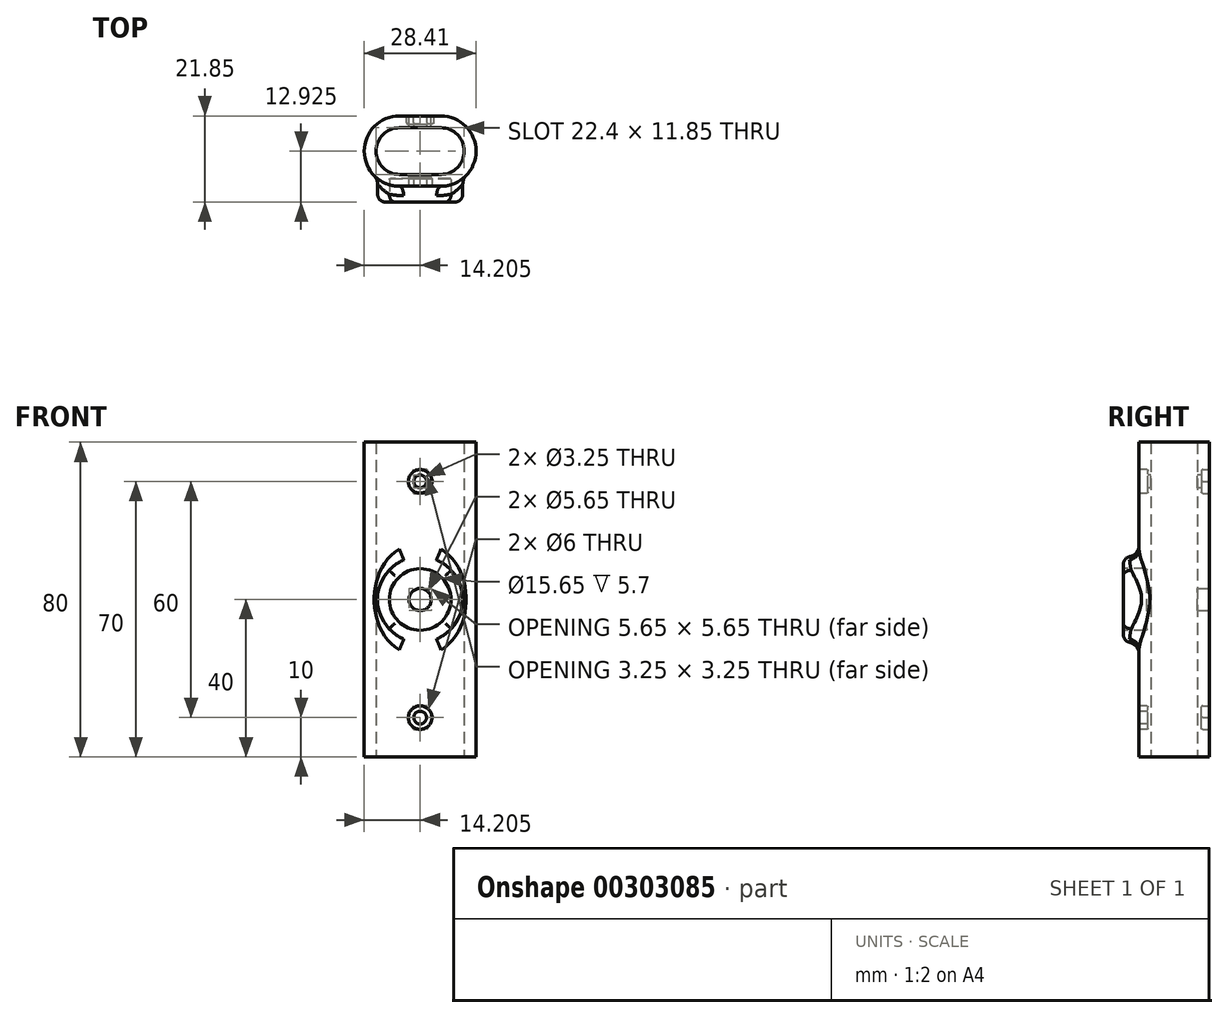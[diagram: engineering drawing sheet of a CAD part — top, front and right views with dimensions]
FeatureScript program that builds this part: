
annotation { "Feature Type Name" : "Feature", "Feature Type Description" : "" }
export const myFeature = defineFeature(function(context is Context, id is Id, definition is map)
    precondition{}
    {
        {
            var Q0;
            Q0=qCreatedBy(makeId("Top.planeOp"),FACE);
            var sketch = newSketch(context, id + "F0", { "sketchPlane" : qUnion([Q0])});
            skLineSegment(sketch, "E0", {"start": v(0, 0) * mm, "end": v(10.55, 0) * mm});
            skLineSegment(sketch, "E1", {"start": v(10.55, 0) * mm, "end": v(10.55, 11.85) * mm, "construction": true});
            skLineSegment(sketch, "E2", {"start": v(10.55, 11.85) * mm, "end": v(0, 11.85) * mm});
            skLineSegment(sketch, "E3", {"start": v(0, 11.85) * mm, "end": v(0, 0) * mm, "construction": true});
            skArc(sketch, "E4", {"start": v(0, 11.85) * mm, "mid": v(-5.92, 5.92) * mm, "end": v(0, 0) * mm});
            skArc(sketch, "E5", {"start": v(10.55, 0) * mm, "mid": v(16.48, 5.92) * mm, "end": v(10.55, 11.85) * mm});
            skArc(sketch, "E6.0", {"start": v(10.55, -3) * mm, "mid": v(19.48, 5.92) * mm, "end": v(10.55, 14.85) * mm});
            skLineSegment(sketch, "E6.1", {"start": v(0, -3) * mm, "end": v(10.55, -3) * mm});
            skArc(sketch, "E6.2", {"start": v(0, 14.85) * mm, "mid": v(-8.92, 5.92) * mm, "end": v(0, -3) * mm});
            skLineSegment(sketch, "E6.3", {"start": v(10.55, 14.85) * mm, "end": v(0, 14.85) * mm});
            skSolve(sketch);
        }
        {
            var Q0;
            Q0 = qSketchRegion(id + "F0", true);
            extrude(context, id + "F1", {"entities" : qUnion([Q0]), "depth" : 80 * mm});
        }
        {
            var Q0;
            Q0=makeQuery(id+"F1.opExtrude","SWEPT_FACE",FACE,{"disambiguationData":[OSD([sQuery(id+"F0.wireOp",EDGE,"E6.1")])]});
            var sketch = newSketch(context, id + "F2", { "sketchPlane" : qUnion([Q0])});
            skLineSegment(sketch, "E7", {"start": v(5.28, 80) * mm, "end": v(5.28, 0) * mm, "construction": true});
            skCircle(sketch, "E8", {"center": v(5.28, 40) * mm, "radius": 2.83 * mm});
            skCircle(sketch, "E9.0", {"center": v(5.28, 40) * mm, "radius": 7.83 * mm});
            skSolve(sketch);
        }
        {
            var Q0;
            Q0 = qSketchRegion(id + "F2", true);
            extrude(context, id + "F3", {"entities" : qUnion([Q0]), "operationType" : NewBodyOperationType.REMOVE, "oppositeDirection" : true, "depth" : 2 * mm});
        }
        {
            var Q0;
            Q0=makeQuery(id+"F3.boolean.opBoolean","SPLIT",FACE,{"disambiguationData":[TD([makeQuery(id+"F3.opExtrude","SWEPT_FACE",FACE,{"disambiguationData":[OSD([sQuery(id+"F2.wireOp",EDGE,"E8")])]})])],"derivedFrom":makeQuery(id+"F1.opExtrude","SWEPT_FACE",FACE,{"disambiguationData":[OSD([sQuery(id+"F0.wireOp",EDGE,"E6.1")])]})});
            var sketch = newSketch(context, id + "F4", { "sketchPlane" : qUnion([Q0])});
            skCircle(sketch, "E10.0", {"center": v(5.28, 40) * mm, "radius": 2.83 * mm});
            skSolve(sketch);
        }
        {
            var Q0;
            {var subQ0=sQuery(id+"F0.wireOp",EDGE,"E6.3");Q0=makeQuery(id+"FMyvibjdp0zur42_1.boolean.opBoolean","MERGE",FACE,{"derivedFrom":[makeQuery(id+"F1.opExtrude","SWEPT_FACE",FACE,{"disambiguationData":[OSD([subQ0])]}),makeQuery(id+"FMyvibjdp0zur42_1.opExtrude","CAP_FACE",FACE,{"disambiguationData":[OSD([sQuery(id+"F0.wireOp",EDGE,"E6.0"),sQuery(id+"F0.wireOp",EDGE,"E6.2"),subQ0,sQuery(id+"FD1jFQHwt7L9kPk_1.wireOp",EDGE,"1de0a669-c472-4eb5-80c6-1d11bea853cf.0"),sQuery(id+"FD1jFQHwt7L9kPk_1.wireOp",EDGE,"1de0a669-c472-4eb5-80c6-1d11bea853cf.3"),sQuery(id+"FD1jFQHwt7L9kPk_1.wireOp",EDGE,"1de0a669-c472-4eb5-80c6-1d11bea853cf.4"),sQuery(id+"FD1jFQHwt7L9kPk_1.wireOp",EDGE,"1de0a669-c472-4eb5-80c6-1d11bea853cf.5"),sQuery(id+"FD1jFQHwt7L9kPk_1.wireOp",EDGE,"1de0a669-c472-4eb5-80c6-1d11bea853cf.6"),sQuery(id+"FD1jFQHwt7L9kPk_1.wireOp",EDGE,"1de0a669-c472-4eb5-80c6-1d11bea853cf.7")])],"isStart":true})]});}
            var sketch = newSketch(context, id + "F5", { "sketchPlane" : qUnion([Q0])});
            skCircle(sketch, "E11.0", {"center": v(-5.28, 40) * mm, "radius": 2.83 * mm});
            skSolve(sketch);
        }
        {
            var Q0;
            Q0 = qSketchRegion(id + "F5", true);
            extrude(context, id + "F6", {"entities" : qUnion([Q0]), "operationType" : NewBodyOperationType.REMOVE, "endBound" : BoundingType.THROUGH_ALL, "oppositeDirection" : true, "depth" : 25 * mm});
        }
        {
            var Q0;
            Q0=makeQuery(id+"F4.imprint","IMPRINT",FACE,{"disambiguationData":[TD([[makeQuery(id+"F4.imprint","IMPRINT",EDGE,{"derivedFrom":sQuery(id+"F4.wireOp",EDGE,"E10.0")}),1.0]])]});
            extrude(context, id + "F7", {"entities" : qUnion([Q0]), "operationType" : NewBodyOperationType.REMOVE, "oppositeDirection" : true, "depth" : 25 * mm});
        }
        {
            var Q0;
            {var subQ0=sQuery(id+"F0.wireOp",EDGE,"E6.2");var subQ1=sQuery(id+"F0.wireOp",EDGE,"E6.1");var subQ2=sQuery(id+"F0.wireOp",EDGE,"E6.0");Q0=makeQuery(id+"F3.boolean.opBoolean","SPLIT",FACE,{"disambiguationData":[TD([makeQuery(id+"F1.opExtrude","CAP_FACE",FACE,{"disambiguationData":[OSD([sQuery(id+"F0.wireOp",EDGE,"E0"),sQuery(id+"F0.wireOp",EDGE,"E2"),sQuery(id+"F0.wireOp",EDGE,"E4"),sQuery(id+"F0.wireOp",EDGE,"E5"),subQ2,subQ1,subQ0,sQuery(id+"F0.wireOp",EDGE,"E6.3")])],"isStart":false})])],"derivedFrom":makeQuery(id+"F1.opExtrude","SWEPT_FACE",FACE,{"disambiguationData":[OSD([subQ1])]})});}
            var sketch = newSketch(context, id + "F8", { "sketchPlane" : qUnion([Q0])});
            skLineSegment(sketch, "E12", {"start": v(5.28, 80) * mm, "end": v(5.28, 0) * mm, "construction": true});
            skLineSegment(sketch, "E13", {"start": v(25.26, 40) * mm, "end": v(-16.5, 40) * mm, "construction": true});
            skPoint(sketch, "E13.startSnap0", {"position": v(5.28, 40) * mm});
            skCircle(sketch, "E14", {"center": v(5.28, 70) * mm, "radius": 1.63 * mm});
            skCircle(sketch, "E15.MirrorC", {"center": v(5.28, 10) * mm, "radius": 1.63 * mm});
            skSolve(sketch);
        }
        {
            var Q0;
            Q0=makeQuery(id+"F8.imprint","IMPRINT",FACE,{"disambiguationData":[TD([[makeQuery(id+"F8.imprint","IMPRINT",EDGE,{"derivedFrom":sQuery(id+"F8.wireOp",EDGE,"E14")}),1.0]])]});
            var Q1;
            Q1=makeQuery(id+"F8.imprint","IMPRINT",FACE,{"disambiguationData":[TD([[makeQuery(id+"F8.imprint","IMPRINT",EDGE,{"derivedFrom":sQuery(id+"F8.wireOp",EDGE,"E15.MirrorC")}),-1.0]])]});
            extrude(context, id + "F9", {"entities" : qUnion([Q0, Q1]), "operationType" : NewBodyOperationType.REMOVE, "endBound" : BoundingType.THROUGH_ALL, "oppositeDirection" : true, "depth" : 25 * mm});
        }
        {
            var Q0;
            Q0=makeQuery(id+"FMyvibjdp0zur42_1.boolean.opBoolean","MERGE",FACE,{"derivedFrom":[makeQuery(id+"F1.opExtrude","SWEPT_FACE",FACE,{"disambiguationData":[OSD([sQuery(id+"F0.wireOp",EDGE,"E6.3")])]}),makeQuery(id+"FMyvibjdp0zur42_1.opExtrude","CAP_FACE",FACE,{"disambiguationData":[OSD([sQuery(id+"FD1jFQHwt7L9kPk_1.wireOp",EDGE,"1de0a669-c472-4eb5-80c6-1d11bea853cf.3"),sQuery(id+"FD1jFQHwt7L9kPk_1.wireOp",EDGE,"1de0a669-c472-4eb5-80c6-1d11bea853cf.5"),sQuery(id+"FD1jFQHwt7L9kPk_1.wireOp",EDGE,"1de0a669-c472-4eb5-80c6-1d11bea853cf.6"),sQuery(id+"FD1jFQHwt7L9kPk_1.wireOp",EDGE,"1de0a669-c472-4eb5-80c6-1d11bea853cf.7")])],"isStart":true})]});
            var sketch = newSketch(context, id + "F10", { "sketchPlane" : qUnion([Q0])});
            skCircle(sketch, "E16.cCircle", {"center": v(-5.28, 70) * mm, "radius": 3 * mm, "construction": true});
            skLineSegment(sketch, "E16.0", {"start": v(-3.54, 67) * mm, "end": v(-7, 67) * mm});
            skLineSegment(sketch, "E16.1", {"start": v(-7, 67) * mm, "end": v(-8.74, 70) * mm});
            skLineSegment(sketch, "E16.2", {"start": v(-8.74, 70) * mm, "end": v(-7, 73) * mm});
            skLineSegment(sketch, "E16.3", {"start": v(-7, 73) * mm, "end": v(-3.54, 73) * mm});
            skLineSegment(sketch, "E16.4", {"start": v(-3.54, 73) * mm, "end": v(-1.81, 70) * mm});
            skLineSegment(sketch, "E16.5", {"start": v(-1.81, 70) * mm, "end": v(-3.54, 67) * mm});
            skPoint(sketch, "E16.0.midPoint", {"position": v(-5.28, 67) * mm});
            skCircle(sketch, "E17.cCircle", {"center": v(-5.28, 10) * mm, "radius": 3 * mm, "construction": true});
            skLineSegment(sketch, "E17.0", {"start": v(-7, 13) * mm, "end": v(-3.54, 13) * mm});
            skLineSegment(sketch, "E17.1", {"start": v(-3.54, 13) * mm, "end": v(-1.81, 10) * mm});
            skLineSegment(sketch, "E17.2", {"start": v(-1.81, 10) * mm, "end": v(-3.54, 7) * mm});
            skLineSegment(sketch, "E17.3", {"start": v(-3.54, 7) * mm, "end": v(-7, 7) * mm});
            skLineSegment(sketch, "E17.4", {"start": v(-7, 7) * mm, "end": v(-8.74, 10) * mm});
            skLineSegment(sketch, "E17.5", {"start": v(-8.74, 10) * mm, "end": v(-7, 13) * mm});
            skPoint(sketch, "E17.0.midPoint", {"position": v(-5.28, 13) * mm});
            skSolve(sketch);
        }
        {
            var Q0;
            Q0 = qSketchRegion(id + "F10", true);
            extrude(context, id + "F11", {"entities" : qUnion([Q0]), "operationType" : NewBodyOperationType.REMOVE, "oppositeDirection" : true, "depth" : 2 * mm});
        }
        {
            var Q0;
            {var subQ0=sQuery(id+"F0.wireOp",EDGE,"E6.2");var subQ1=sQuery(id+"F0.wireOp",EDGE,"E6.1");var subQ2=sQuery(id+"F0.wireOp",EDGE,"E6.0");Q0=makeQuery(id+"F3.boolean.opBoolean","SPLIT",FACE,{"disambiguationData":[TD([makeQuery(id+"F1.opExtrude","CAP_FACE",FACE,{"disambiguationData":[OSD([sQuery(id+"F0.wireOp",EDGE,"E0"),sQuery(id+"F0.wireOp",EDGE,"E2"),sQuery(id+"F0.wireOp",EDGE,"E4"),sQuery(id+"F0.wireOp",EDGE,"E5"),subQ2,subQ1,subQ0,sQuery(id+"F0.wireOp",EDGE,"E6.3")])],"isStart":false})])],"derivedFrom":makeQuery(id+"F1.opExtrude","SWEPT_FACE",FACE,{"disambiguationData":[OSD([subQ1])]})});}
            var sketch = newSketch(context, id + "F12", { "sketchPlane" : qUnion([Q0])});
            skCircle(sketch, "E18.0", {"center": v(5.28, 70) * mm, "radius": 1.63 * mm});
            skCircle(sketch, "E19.0", {"center": v(5.28, 10) * mm, "radius": 1.63 * mm});
            skCircle(sketch, "E20", {"center": v(5.28, 70) * mm, "radius": 3 * mm});
            skCircle(sketch, "E21", {"center": v(5.28, 10) * mm, "radius": 3 * mm});
            skSolve(sketch);
        }
        {
            var Q0;
            Q0 = qSketchRegion(id + "F12", true);
            extrude(context, id + "F13", {"entities" : qUnion([Q0]), "operationType" : NewBodyOperationType.REMOVE, "oppositeDirection" : true, "depth" : 2.25 * mm});
        }
        {
            var Q0;
            {var subQ0=sQuery(id+"F0.wireOp",EDGE,"E6.2");var subQ1=sQuery(id+"F0.wireOp",EDGE,"E6.1");var subQ2=sQuery(id+"F0.wireOp",EDGE,"E6.0");Q0=makeQuery(id+"F3.boolean.opBoolean","SPLIT",FACE,{"disambiguationData":[TD([makeQuery(id+"F1.opExtrude","CAP_FACE",FACE,{"disambiguationData":[OSD([sQuery(id+"F0.wireOp",EDGE,"E0"),sQuery(id+"F0.wireOp",EDGE,"E2"),sQuery(id+"F0.wireOp",EDGE,"E4"),sQuery(id+"F0.wireOp",EDGE,"E5"),subQ2,subQ1,subQ0,sQuery(id+"F0.wireOp",EDGE,"E6.3")])],"isStart":false})])],"derivedFrom":makeQuery(id+"F1.opExtrude","SWEPT_FACE",FACE,{"disambiguationData":[OSD([subQ1])]})});}
            var sketch = newSketch(context, id + "F14", { "sketchPlane" : qUnion([Q0])});
            skCircle(sketch, "E22.0", {"center": v(5.28, 40) * mm, "radius": 10.83 * mm});
            skCircle(sketch, "E23.0", {"center": v(5.28, 40) * mm, "radius": 7.83 * mm});
            skSolve(sketch);
        }
        {
            var Q0;
            Q0 = qSketchRegion(id + "F14", true);
            var Q1;
            Q1=makeQuery(id+"F1.opExtrude","SWEPT_FACE",FACE,{"disambiguationData":[OSD([sQuery(id+"F0.wireOp",EDGE,"E0")])]});
            extrude(context, id + "F15", {"entities" : qUnion([Q0]), "operationType" : NewBodyOperationType.ADD, "endBound" : BoundingType.UP_TO_SURFACE, "oppositeDirection" : true, "endBoundEntityFace" : qUnion([Q1]), "depth" : 25 * mm, "hasSecondDirection" : true, "secondDirectionOppositeDirection" : false, "secondDirectionDepth" : 4 * mm});
        }
        {
            var Q0;
            Q0=makeQuery(id+"F1.opExtrude","SWEPT_FACE",FACE,{"disambiguationData":[OSD([sQuery(id+"F0.wireOp",EDGE,"E6.3")])]});
            var sketch = newSketch(context, id + "F16", { "sketchPlane" : qUnion([Q0])});
            skCircle(sketch, "E24", {"center": v(-5.28, 40) * mm, "radius": 11 * mm});
            skCircle(sketch, "E25.0", {"center": v(-5.28, 40) * mm, "radius": 2.83 * mm});
            skSolve(sketch);
        }
        {
            var Q0;
            {var subQ0=sQuery(id+"F16.wireOp",EDGE,"E24");var subQ1=makeQuery(id+"F1.opExtrude","SWEPT_EDGE",EDGE,{"disambiguationData":[OSD([sQuery(id+"F0.wireOp",EDGE,"E6.0"),sQuery(id+"F0.wireOp",EDGE,"E6.3")])]});var subQ2=makeQuery(id+"F16.imprint","INTERSECT",VERTEX,{"disambiguationData":[OD(0.0)],"derivedFrom":[subQ1,subQ0]});Q0=makeQuery(id+"F16.imprint","IMPRINT",FACE,{"disambiguationData":[TD([[makeQuery(id+"F16.imprint","IMPRINT",EDGE,{"disambiguationData":[TD([[subQ2,-1.0]])],"derivedFrom":subQ0}),1.0]])]});}
            var Q1;
            {var subQ0=sQuery(id+"F16.wireOp",EDGE,"E24");var subQ1=makeQuery(id+"F1.opExtrude","SWEPT_EDGE",EDGE,{"disambiguationData":[OSD([sQuery(id+"F0.wireOp",EDGE,"E6.2"),sQuery(id+"F0.wireOp",EDGE,"E6.3")])]});var subQ2=makeQuery(id+"F16.imprint","INTERSECT",VERTEX,{"disambiguationData":[OD(0.0)],"derivedFrom":[subQ1,subQ0]});Q1=makeQuery(id+"F16.imprint","IMPRINT",FACE,{"disambiguationData":[TD([[makeQuery(id+"F16.imprint","IMPRINT",EDGE,{"disambiguationData":[TD([[subQ2,1.0]])],"derivedFrom":subQ0}),1.0]])]});}
            extrude(context, id + "F17", {"entities" : qUnion([Q0, Q1]), "operationType" : NewBodyOperationType.ADD, "endBound" : BoundingType.UP_TO_NEXT, "oppositeDirection" : true, "depth" : 25 * mm});
        }
        {
            var Q0;
            Q0=makeQuery(id+"F15.boolean.opBoolean","INTERSECT",EDGE,{"derivedFrom":[makeQuery(id+"F1.opExtrude","SWEPT_FACE",FACE,{"disambiguationData":[OSD([sQuery(id+"F0.wireOp",EDGE,"E6.2")])]}),makeQuery(id+"F15.opExtrude","SWEPT_FACE",FACE,{"disambiguationData":[OSD([sQuery(id+"F14.wireOp",EDGE,"E22.0")])]})]});
            var Q1;
            {var subQ0=sQuery(id+"F16.wireOp",EDGE,"E24");var subQ1=sQuery(id+"F0.wireOp",EDGE,"E6.2");var subQ2=makeQuery(id+"F1.opExtrude","SWEPT_EDGE",EDGE,{"disambiguationData":[OSD([subQ1,sQuery(id+"F0.wireOp",EDGE,"E6.3")])]});Q1=makeQuery(id+"F17.opExtrude","TWEAK_EDGE",EDGE,{"derivedFrom":[makeQuery(id+"F1.opExtrude","SWEPT_FACE",FACE,{"disambiguationData":[OSD([subQ1])]}),makeQuery(id+"F16.imprint","IMPRINT",EDGE,{"disambiguationData":[TD([[makeQuery(id+"F16.imprint","INTERSECT",VERTEX,{"disambiguationData":[OD(0.0)],"derivedFrom":[subQ2,subQ0]}),1.0]])],"derivedFrom":subQ0})]});}
            var Q2;
            Q2=makeQuery(id+"F17.opExtrude","CAP_EDGE",EDGE,{"disambiguationData":[OSD([sQuery(id+"F16.wireOp",EDGE,"E24")])],"isStart":false});
            fillet(context, id + "F18", {"entities" : qUnion([Q0, Q1, Q2]), "radius" : 3 * mm, "tangentPropagation" : true, "allowEdgeOverflow" : false});
        }
        {
            var Q0;
            Q0=makeQuery(id+"F15.opExtrude","CAP_EDGE",EDGE,{"disambiguationData":[OSD([sQuery(id+"F14.wireOp",EDGE,"E22.0")])],"isStart":true});
            fillet(context, id + "F19", {"entities" : qUnion([Q0]), "radius" : 2 * mm, "tangentPropagation" : true, "allowEdgeOverflow" : false});
        }
        {
            var Q0;
            Q0=makeQuery(id+"F13.boolean.opBoolean","COPY",EDGE,{"derivedFrom":makeQuery(id+"F13.opExtrude","CAP_EDGE",EDGE,{"disambiguationData":[OSD([sQuery(id+"F12.wireOp",EDGE,"E20")])],"isStart":false})});
            var Q1;
            Q1=makeQuery(id+"F13.boolean.opBoolean","COPY",EDGE,{"derivedFrom":makeQuery(id+"F13.opExtrude","CAP_EDGE",EDGE,{"disambiguationData":[OSD([sQuery(id+"F12.wireOp",EDGE,"E21")])],"isStart":false})});
            var Q2;
            Q2=makeQuery(id+"F3.boolean.opBoolean","COPY",EDGE,{"derivedFrom":makeQuery(id+"F3.opExtrude","CAP_EDGE",EDGE,{"disambiguationData":[OSD([sQuery(id+"F2.wireOp",EDGE,"E9.0")])],"isStart":false})});
            var Q3;
            Q3=makeQuery(id+"F11.boolean.opBoolean","COPY",EDGE,{"derivedFrom":makeQuery(id+"F11.opExtrude","CAP_EDGE",EDGE,{"disambiguationData":[OSD([sQuery(id+"F10.wireOp",EDGE,"E17.2")])],"isStart":false})});
            var Q4;
            Q4=makeQuery(id+"F11.boolean.opBoolean","COPY",EDGE,{"derivedFrom":makeQuery(id+"F11.opExtrude","CAP_EDGE",EDGE,{"disambiguationData":[OSD([sQuery(id+"F10.wireOp",EDGE,"E17.1")])],"isStart":false})});
            var Q5;
            Q5=makeQuery(id+"F11.boolean.opBoolean","COPY",EDGE,{"derivedFrom":makeQuery(id+"F11.opExtrude","CAP_EDGE",EDGE,{"disambiguationData":[OSD([sQuery(id+"F10.wireOp",EDGE,"E17.5")])],"isStart":false})});
            var Q6;
            Q6=makeQuery(id+"F11.boolean.opBoolean","COPY",EDGE,{"derivedFrom":makeQuery(id+"F11.opExtrude","CAP_EDGE",EDGE,{"disambiguationData":[OSD([sQuery(id+"F10.wireOp",EDGE,"E17.4")])],"isStart":false})});
            var Q7;
            Q7=makeQuery(id+"F11.boolean.opBoolean","COPY",EDGE,{"derivedFrom":makeQuery(id+"F11.opExtrude","CAP_EDGE",EDGE,{"disambiguationData":[OSD([sQuery(id+"F10.wireOp",EDGE,"E17.0")])],"isStart":false})});
            var Q8;
            Q8=makeQuery(id+"F11.boolean.opBoolean","COPY",EDGE,{"derivedFrom":makeQuery(id+"F11.opExtrude","CAP_EDGE",EDGE,{"disambiguationData":[OSD([sQuery(id+"F10.wireOp",EDGE,"E17.3")])],"isStart":false})});
            var Q9;
            Q9=makeQuery(id+"F11.boolean.opBoolean","COPY",EDGE,{"derivedFrom":makeQuery(id+"F11.opExtrude","CAP_EDGE",EDGE,{"disambiguationData":[OSD([sQuery(id+"F10.wireOp",EDGE,"E16.1")])],"isStart":false})});
            var Q10;
            Q10=makeQuery(id+"F11.boolean.opBoolean","COPY",EDGE,{"derivedFrom":makeQuery(id+"F11.opExtrude","CAP_EDGE",EDGE,{"disambiguationData":[OSD([sQuery(id+"F10.wireOp",EDGE,"E16.0")])],"isStart":false})});
            var Q11;
            Q11=makeQuery(id+"F11.boolean.opBoolean","COPY",EDGE,{"derivedFrom":makeQuery(id+"F11.opExtrude","CAP_EDGE",EDGE,{"disambiguationData":[OSD([sQuery(id+"F10.wireOp",EDGE,"E16.2")])],"isStart":false})});
            var Q12;
            Q12=makeQuery(id+"F11.boolean.opBoolean","COPY",EDGE,{"derivedFrom":makeQuery(id+"F11.opExtrude","CAP_EDGE",EDGE,{"disambiguationData":[OSD([sQuery(id+"F10.wireOp",EDGE,"E16.3")])],"isStart":false})});
            var Q13;
            Q13=makeQuery(id+"F11.boolean.opBoolean","COPY",EDGE,{"derivedFrom":makeQuery(id+"F11.opExtrude","CAP_EDGE",EDGE,{"disambiguationData":[OSD([sQuery(id+"F10.wireOp",EDGE,"E16.4")])],"isStart":false})});
            var Q14;
            Q14=makeQuery(id+"F11.boolean.opBoolean","COPY",EDGE,{"derivedFrom":makeQuery(id+"F11.opExtrude","CAP_EDGE",EDGE,{"disambiguationData":[OSD([sQuery(id+"F10.wireOp",EDGE,"E16.5")])],"isStart":false})});
            var Q15;
            {var subQ0=sQuery(id+"F16.wireOp",EDGE,"E24");var subQ1=sQuery(id+"F0.wireOp",EDGE,"E6.3");Q15=makeQuery(id+"F18.opFillet","BLEND_EDGE",EDGE,{"disambiguationData":[OD(1.0)],"blendedFrom":[makeQuery(id+"F17.opExtrude","CAP_EDGE",EDGE,{"disambiguationData":[OSD([subQ0])],"isStart":false}),makeQuery(id+"F17.boolean.opBoolean","MERGE",FACE,{"derivedFrom":[makeQuery(id+"F1.opExtrude","SWEPT_FACE",FACE,{"disambiguationData":[OSD([subQ1])]}),makeQuery(id+"F17.opExtrude","CAP_FACE",FACE,{"disambiguationData":[OSD([sQuery(id+"F0.wireOp",EDGE,"E6.0"),subQ1,subQ0])],"isStart":true}),makeQuery(id+"F17.opExtrude","CAP_FACE",FACE,{"disambiguationData":[OSD([sQuery(id+"F0.wireOp",EDGE,"E6.2"),subQ1,subQ0])],"isStart":true})]})],"blendedInto":[makeQuery(id+"F17.boolean.opBoolean","MERGE",FACE,{"derivedFrom":[makeQuery(id+"F1.opExtrude","SWEPT_FACE",FACE,{"disambiguationData":[OSD([subQ1])]}),makeQuery(id+"F17.opExtrude","CAP_FACE",FACE,{"disambiguationData":[OSD([sQuery(id+"F0.wireOp",EDGE,"E6.0"),subQ1,subQ0])],"isStart":true}),makeQuery(id+"F17.opExtrude","CAP_FACE",FACE,{"disambiguationData":[OSD([sQuery(id+"F0.wireOp",EDGE,"E6.2"),subQ1,subQ0])],"isStart":true})]})]});}
            var Q16;
            {var subQ0=sQuery(id+"F16.wireOp",EDGE,"E24");var subQ1=sQuery(id+"F0.wireOp",EDGE,"E6.3");Q16=makeQuery(id+"F18.opFillet","BLEND_EDGE",EDGE,{"disambiguationData":[OD(0.0)],"blendedFrom":[makeQuery(id+"F17.opExtrude","CAP_EDGE",EDGE,{"disambiguationData":[OSD([subQ0])],"isStart":false}),makeQuery(id+"F17.boolean.opBoolean","MERGE",FACE,{"derivedFrom":[makeQuery(id+"F1.opExtrude","SWEPT_FACE",FACE,{"disambiguationData":[OSD([subQ1])]}),makeQuery(id+"F17.opExtrude","CAP_FACE",FACE,{"disambiguationData":[OSD([sQuery(id+"F0.wireOp",EDGE,"E6.0"),subQ1,subQ0])],"isStart":true}),makeQuery(id+"F17.opExtrude","CAP_FACE",FACE,{"disambiguationData":[OSD([sQuery(id+"F0.wireOp",EDGE,"E6.2"),subQ1,subQ0])],"isStart":true})]})],"blendedInto":[makeQuery(id+"F17.boolean.opBoolean","MERGE",FACE,{"derivedFrom":[makeQuery(id+"F1.opExtrude","SWEPT_FACE",FACE,{"disambiguationData":[OSD([subQ1])]}),makeQuery(id+"F17.opExtrude","CAP_FACE",FACE,{"disambiguationData":[OSD([sQuery(id+"F0.wireOp",EDGE,"E6.0"),subQ1,subQ0])],"isStart":true}),makeQuery(id+"F17.opExtrude","CAP_FACE",FACE,{"disambiguationData":[OSD([sQuery(id+"F0.wireOp",EDGE,"E6.2"),subQ1,subQ0])],"isStart":true})]})]});}
            var Q17;
            {var subQ0=sQuery(id+"F16.wireOp",EDGE,"E24");var subQ1=makeQuery(id+"F1.opExtrude","SWEPT_EDGE",EDGE,{"disambiguationData":[OSD([sQuery(id+"F0.wireOp",EDGE,"E6.0"),sQuery(id+"F0.wireOp",EDGE,"E6.3")])]});Q17=makeQuery(id+"F17.opExtrude","CAP_EDGE",EDGE,{"disambiguationData":[OSD([subQ0]),TDD([makeQuery(id+"F16.imprint","IMPRINT",EDGE,{"disambiguationData":[TD([[makeQuery(id+"F16.imprint","INTERSECT",VERTEX,{"disambiguationData":[OD(0.0)],"derivedFrom":[subQ1,subQ0]}),-1.0]])],"derivedFrom":subQ0})])],"isStart":true});}
            var Q18;
            {var subQ0=sQuery(id+"F16.wireOp",EDGE,"E24");var subQ1=makeQuery(id+"F1.opExtrude","SWEPT_EDGE",EDGE,{"disambiguationData":[OSD([sQuery(id+"F0.wireOp",EDGE,"E6.2"),sQuery(id+"F0.wireOp",EDGE,"E6.3")])]});Q18=makeQuery(id+"F17.opExtrude","CAP_EDGE",EDGE,{"disambiguationData":[OSD([subQ0]),TDD([makeQuery(id+"F16.imprint","IMPRINT",EDGE,{"disambiguationData":[TD([[makeQuery(id+"F16.imprint","INTERSECT",VERTEX,{"disambiguationData":[OD(0.0)],"derivedFrom":[subQ1,subQ0]}),1.0]])],"derivedFrom":subQ0})])],"isStart":true});}
            var Q19;
            {var subQ0=sQuery(id+"F16.wireOp",EDGE,"E24");var subQ1=sQuery(id+"F0.wireOp",EDGE,"E6.3");var subQ2=sQuery(id+"F0.wireOp",EDGE,"E6.2");var subQ3=makeQuery(id+"F1.opExtrude","SWEPT_EDGE",EDGE,{"disambiguationData":[OSD([subQ2,subQ1])]});Q19=makeQuery(id+"F18.opFillet","BLEND_EDGE",EDGE,{"disambiguationData":[OD(1.0)],"blendedFrom":[makeQuery(id+"F17.opExtrude","TWEAK_EDGE",EDGE,{"derivedFrom":[makeQuery(id+"F1.opExtrude","SWEPT_FACE",FACE,{"disambiguationData":[OSD([subQ2])]}),makeQuery(id+"F16.imprint","IMPRINT",EDGE,{"disambiguationData":[TD([[makeQuery(id+"F16.imprint","INTERSECT",VERTEX,{"disambiguationData":[OD(0.0)],"derivedFrom":[subQ3,subQ0]}),1.0]])],"derivedFrom":subQ0})]}),makeQuery(id+"F17.boolean.opBoolean","MERGE",FACE,{"derivedFrom":[makeQuery(id+"F1.opExtrude","SWEPT_FACE",FACE,{"disambiguationData":[OSD([subQ1])]}),makeQuery(id+"F17.opExtrude","CAP_FACE",FACE,{"disambiguationData":[OSD([sQuery(id+"F0.wireOp",EDGE,"E6.0"),subQ1,subQ0])],"isStart":true}),makeQuery(id+"F17.opExtrude","CAP_FACE",FACE,{"disambiguationData":[OSD([subQ2,subQ1,subQ0])],"isStart":true})]})],"blendedInto":[makeQuery(id+"F17.boolean.opBoolean","MERGE",FACE,{"derivedFrom":[makeQuery(id+"F1.opExtrude","SWEPT_FACE",FACE,{"disambiguationData":[OSD([subQ1])]}),makeQuery(id+"F17.opExtrude","CAP_FACE",FACE,{"disambiguationData":[OSD([sQuery(id+"F0.wireOp",EDGE,"E6.0"),subQ1,subQ0])],"isStart":true}),makeQuery(id+"F17.opExtrude","CAP_FACE",FACE,{"disambiguationData":[OSD([subQ2,subQ1,subQ0])],"isStart":true})]})]});}
            fillet(context, id + "F20", {"entities" : qUnion([Q0, Q1, Q2, Q3, Q4, Q5, Q6, Q7, Q8, Q9, Q10, Q11, Q12, Q13, Q14, Q15, Q16, Q17, Q18, Q19]), "radius" : .3 * mm, "tangentPropagation" : true, "allowEdgeOverflow" : false});
        }
    });
